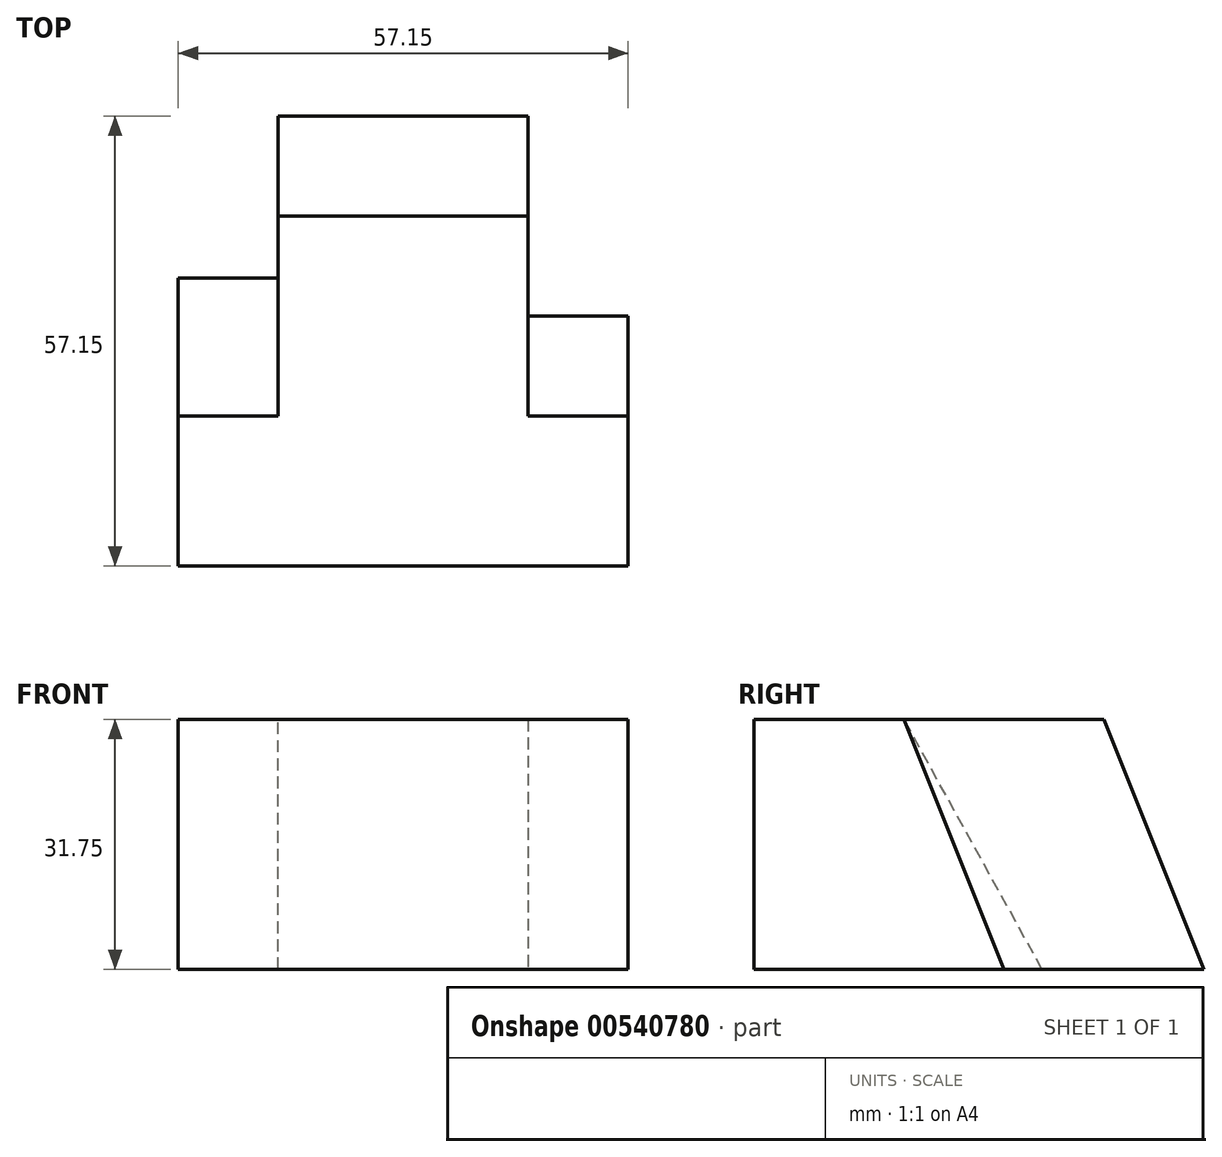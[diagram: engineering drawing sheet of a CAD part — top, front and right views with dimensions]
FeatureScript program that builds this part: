
annotation { "Feature Type Name" : "Feature", "Feature Type Description" : "" }
export const myFeature = defineFeature(function(context is Context, id is Id, definition is map)
    precondition{}
    {
        {
            var Q0;
            Q0=qCreatedBy(makeId("Right.planeOp"),FACE);
            var sketch = newSketch(context, id + "F0", { "sketchPlane" : qUnion([Q0])});
            skLineSegment(sketch, "E0", {"start": v(0, 0) * mm, "end": v(0, 31.75) * mm});
            skLineSegment(sketch, "E1", {"start": v(0, 31.75) * mm, "end": v(57.15, 31.75) * mm});
            skLineSegment(sketch, "E2", {"start": v(57.15, 31.75) * mm, "end": v(57.15, 0) * mm});
            skLineSegment(sketch, "E3", {"start": v(57.15, 0) * mm, "end": v(0, 0) * mm});
            skLineSegment(sketch, "E4", {"start": v(57.15, 0) * mm, "end": v(31.75, 0) * mm});
            skLineSegment(sketch, "E5", {"start": v(0, 31.75) * mm, "end": v(19.05, 31.75) * mm});
            skLineSegment(sketch, "E6", {"start": v(19.05, 31.75) * mm, "end": v(31.75, 0) * mm});
            skSolve(sketch);
        }
        {
            var Q0;
            Q0=makeQuery(id+"F0.imprint","IMPRINT",FACE,{"disambiguationData":[TD([[makeQuery(id+"F0.imprint","IMPRINT",EDGE,{"derivedFrom":sQuery(id+"F0.wireOp",EDGE,"E0")}),-1.0]])]});
            var Q1;
            Q1=makeQuery(id+"F0.imprint","IMPRINT",FACE,{"disambiguationData":[TD([[makeQuery(id+"F0.imprint","IMPRINT",EDGE,{"derivedFrom":sQuery(id+"F0.wireOp",EDGE,"E1")}),-1.0]])]});
            extrude(context, id + "F1", {"entities" : qUnion([Q0, Q1]), "depth" : 25.4 * mm, "offsetDistance" : 25.4 * mm});
        }
        {
            var Q0;
            Q0=makeQuery(id+"F1.opExtrude","CAP_FACE",FACE,{"disambiguationData":[OSD([sQuery(id+"F0.wireOp",EDGE,"E0"),sQuery(id+"F0.wireOp",EDGE,"E1"),sQuery(id+"F0.wireOp",EDGE,"E2"),sQuery(id+"F0.wireOp",EDGE,"E3"),sQuery(id+"F0.wireOp",EDGE,"E4"),sQuery(id+"F0.wireOp",EDGE,"E5")])],"isStart":false});
            var sketch = newSketch(context, id + "F2", { "sketchPlane" : qUnion([Q0])});
            skLineSegment(sketch, "E7", {"start": v(0, 31.75) * mm, "end": v(19.05, 31.75) * mm});
            skLineSegment(sketch, "E8", {"start": v(57.15, 0) * mm, "end": v(31.75, 0) * mm});
            skLineSegment(sketch, "E9", {"start": v(31.75, 0) * mm, "end": v(19.05, 31.75) * mm});
            skSolve(sketch);
        }
        {
            var Q0;
            Q0=makeQuery(id+"F2.imprint","IMPRINT",FACE,{"disambiguationData":[TD([[makeQuery(id+"F2.imprint","IMPRINT",EDGE,{"derivedFrom":sQuery(id+"F2.wireOp",EDGE,"E8")}),-1.0]])]});
            extrude(context, id + "F3", {"entities" : qUnion([Q0]), "operationType" : NewBodyOperationType.REMOVE, "oppositeDirection" : true, "depth" : 12.7 * mm, "offsetDistance" : 25.4 * mm});
        }
        {
            var Q0;
            Q0=makeQuery(id+"F1.opExtrude","CAP_FACE",FACE,{"disambiguationData":[OSD([sQuery(id+"F0.wireOp",EDGE,"E0"),sQuery(id+"F0.wireOp",EDGE,"E1"),sQuery(id+"F0.wireOp",EDGE,"E2"),sQuery(id+"F0.wireOp",EDGE,"E3"),sQuery(id+"F0.wireOp",EDGE,"E4"),sQuery(id+"F0.wireOp",EDGE,"E5")])],"isStart":true});
            var sketch = newSketch(context, id + "F4", { "sketchPlane" : qUnion([Q0])});
            skLineSegment(sketch, "E10", {"start": v(-57.15, 0) * mm, "end": v(-36.6, 0) * mm});
            skLineSegment(sketch, "E11", {"start": v(0, 31.75) * mm, "end": v(-19.05, 31.75) * mm});
            skLineSegment(sketch, "E12", {"start": v(-36.6, 0) * mm, "end": v(-19.05, 31.75) * mm});
            skSolve(sketch);
        }
        {
            var Q0;
            Q0=makeQuery(id+"F3.boolean.opBoolean","COPY",FACE,{"derivedFrom":makeQuery(id+"F3.opExtrude","CAP_FACE",FACE,{"disambiguationData":[OSD([sQuery(id+"F0.wireOp",EDGE,"E1"),sQuery(id+"F0.wireOp",EDGE,"E2"),sQuery(id+"F0.wireOp",EDGE,"E5"),sQuery(id+"F2.wireOp",EDGE,"E8"),sQuery(id+"F2.wireOp",EDGE,"E9")])],"isStart":false})});
            var Q1;
            Q1=makeQuery(id+"F1.opExtrude","CAP_FACE",FACE,{"disambiguationData":[OSD([sQuery(id+"F0.wireOp",EDGE,"E0"),sQuery(id+"F0.wireOp",EDGE,"E1"),sQuery(id+"F0.wireOp",EDGE,"E2"),sQuery(id+"F0.wireOp",EDGE,"E3"),sQuery(id+"F0.wireOp",EDGE,"E4"),sQuery(id+"F0.wireOp",EDGE,"E5")])],"isStart":false});
            extrude(context, id + "F5", {"entities" : qUnion([Q0, Q1]), "operationType" : NewBodyOperationType.ADD, "depth" : 31.75 * mm, "offsetDistance" : 25.4 * mm});
        }
        {
            var Q0;
            Q0=makeQuery(id+"F4.imprint","IMPRINT",FACE,{"disambiguationData":[TD([[makeQuery(id+"F4.imprint","IMPRINT",EDGE,{"derivedFrom":sQuery(id+"F4.wireOp",EDGE,"E10")}),1.0]])]});
            extrude(context, id + "F6", {"entities" : qUnion([Q0]), "operationType" : NewBodyOperationType.REMOVE, "oppositeDirection" : true, "depth" : 12.7 * mm, "offsetDistance" : 25.4 * mm});
        }
        {
            var Q0;
            Q0=makeQuery(id+"F5.opExtrude","CAP_FACE",FACE,{"disambiguationData":[OSD([sQuery(id+"F0.wireOp",EDGE,"E1"),sQuery(id+"F0.wireOp",EDGE,"E2"),sQuery(id+"F0.wireOp",EDGE,"E5"),sQuery(id+"F2.wireOp",EDGE,"E8"),sQuery(id+"F2.wireOp",EDGE,"E9")])],"isStart":false});
            var sketch = newSketch(context, id + "F7", { "sketchPlane" : qUnion([Q0])});
            skLineSegment(sketch, "E13", {"start": v(31.75, 0) * mm, "end": v(44.45, 0) * mm});
            skLineSegment(sketch, "E14", {"start": v(44.45, 0) * mm, "end": v(44.45, 31.75) * mm});
            skLineSegment(sketch, "E15", {"start": v(44.45, 31.75) * mm, "end": v(57.15, 0) * mm});
            skSolve(sketch);
        }
        {
            var Q0;
            {var subQ0=sQuery(id+"F7.wireOp",EDGE,"E15");Q0=makeQuery(id+"F7.imprint","IMPRINT",FACE,{"disambiguationData":[TD([[makeQuery(id+"F7.imprint","IMPRINT",EDGE,{"derivedFrom":subQ0}),1.0]])]});}
            extrude(context, id + "F8", {"entities" : qUnion([Q0]), "operationType" : NewBodyOperationType.REMOVE, "oppositeDirection" : true, "depth" : 12.7 * mm, "offsetDistance" : 25.4 * mm});
        }
        {
            var Q0;
            Q0=makeQuery(id+"F8.boolean.opBoolean","COPY",FACE,{"derivedFrom":makeQuery(id+"F8.opExtrude","CAP_FACE",FACE,{"disambiguationData":[OSD([sQuery(id+"F0.wireOp",EDGE,"E1"),sQuery(id+"F0.wireOp",EDGE,"E2"),sQuery(id+"F0.wireOp",EDGE,"E5"),sQuery(id+"F7.wireOp",EDGE,"E15")])],"isStart":false})});
            extrude(context, id + "F9", {"entities" : qUnion([Q0]), "operationType" : NewBodyOperationType.REMOVE, "oppositeDirection" : true, "depth" : 25.4 * mm, "offsetDistance" : 25.4 * mm});
        }
    });
